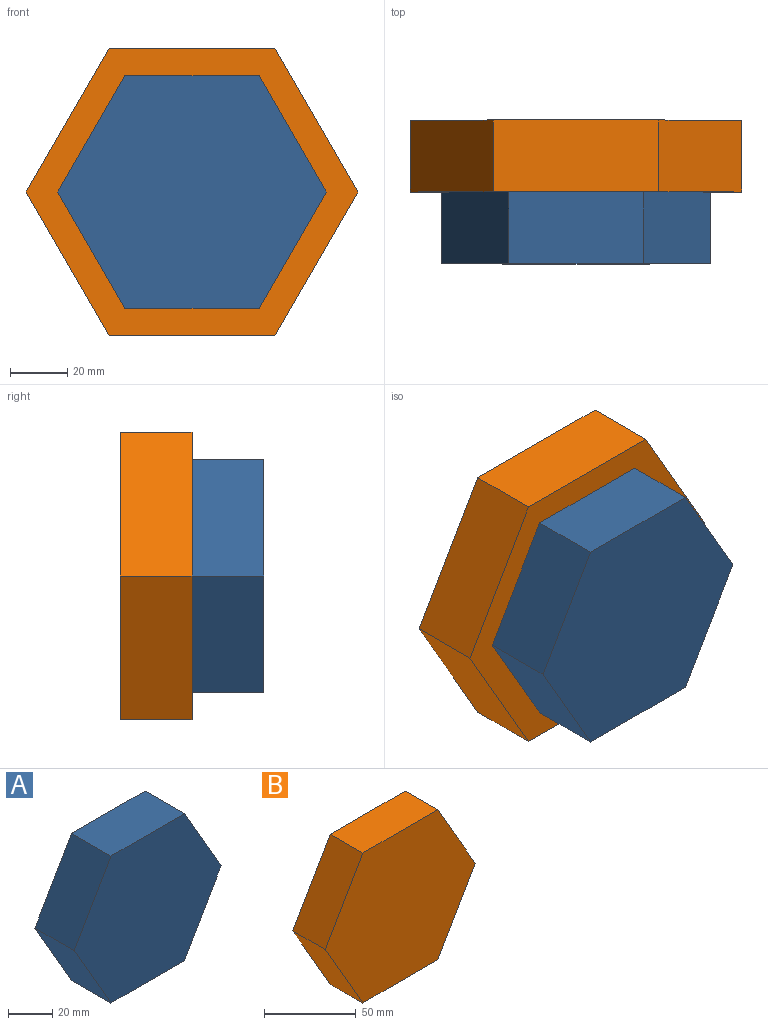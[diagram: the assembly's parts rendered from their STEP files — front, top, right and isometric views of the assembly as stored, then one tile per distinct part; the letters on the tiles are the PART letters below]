
ASSEMBLY  parts=2 mates=1
PART A: 8 faces, bbox 93.5x25x80.9 mm
  f0: plane 46.73x25mm, normal (0,0,-1), area 1168.4mm2, adj f1,f5,f6,f7
  f1: plane 40.47x25mm, normal (0.87,0,-0.5), area 1168.4mm2, adj f0,f2,f6,f7
  f2: plane 40.47x25mm, normal (0.87,0,0.5), area 1168.4mm2, adj f1,f3,f6,f7
  f3: plane 46.73x25mm, normal (0,0,1), area 1168.4mm2, adj f2,f4,f6,f7
  f4: plane 40.47x25mm, normal (-0.87,0,0.5), area 1168.4mm2, adj f3,f5,f6,f7
  f5: plane 40.47x25mm, normal (-0.87,0,-0.5), area 1168.4mm2, adj f0,f4,f6,f7
  f6: plane 93.47x80.95mm, normal (0,-1,0), area 5674.4mm2, adj f0,f1,f2,f3,f4,f5
  f7: plane 93.47x80.95mm, normal (0,1,0), area 5674.4mm2, adj f0,f1,f2,f3,f4,f5
PART B: 8 faces, bbox 115.5x25x100 mm
  f0: plane 57.74x25mm, normal (0,0,-1), area 1443.4mm2, adj f1,f5,f6,f7
  f1: plane 50x28.87mm, normal (0.87,0,-0.5), area 1443.4mm2, adj f0,f2,f6,f7
  f2: plane 50x28.87mm, normal (0.87,0,0.5), area 1443.4mm2, adj f1,f3,f6,f7
  f3: plane 57.74x25mm, normal (0,0,1), area 1443.4mm2, adj f2,f4,f6,f7
  f4: plane 50x28.87mm, normal (-0.87,0,0.5), area 1443.4mm2, adj f3,f5,f6,f7
  f5: plane 50x28.87mm, normal (-0.87,0,-0.5), area 1443.4mm2, adj f0,f4,f6,f7
  f6: plane 115.47x100mm, normal (0,-1,0), area 8660.3mm2, adj f0,f1,f2,f3,f4,f5
  f7: plane 115.47x100mm, normal (0,1,0), area 8660.3mm2, adj f0,f1,f2,f3,f4,f5
PLACE A rot(axis=(1,0,0),180deg) t=(-2.12,-93.95,-82.84)mm
PLACE B t=(-2.12,-43.95,-82.84)mm
MATE revolute A.f6 <-> B.f6  axis (0,1,0) through (-2.12,-68.95,-82.84)mm
